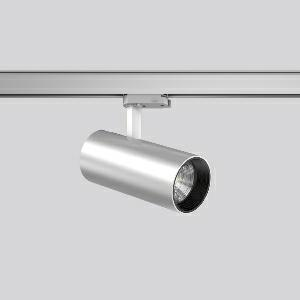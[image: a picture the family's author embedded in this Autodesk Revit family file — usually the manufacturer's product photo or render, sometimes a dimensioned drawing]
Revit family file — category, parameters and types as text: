
# Revit family: deecos_s_mini_742201_004_3_7e94
name_source: partatom
category: Lighting Fixtures
units: mm (PartAtom-declared; Revit-internal decimal feet)

## family parameters
Cut with Voids When Loaded = No
Host = Face
Light Source = No
Part Type = Normal
Room Calculation Point = No
Round Connector Dimension = Use Diameter
Shared = No

## types (1)
- DEECOS S mini (1 x LED Modul 935, 2300 lm, 3500)
    Apparent Load = 20 VA
    Approval mark = CE
    CIE Flux Codes = 80 99 100 100 100
    Color Rendering = 92
    Color Temperature = 3500
    Default Elevation = 1800 mm
    Description = Series: DEECOS S mini
LED surface-mounted projector in modern design with no visible cooling ribs. Housing: die-cast aluminium, powder-coated. Rotation range: 356°. Swivel range: 90°. Black plastic ring and recessed LED to prevent glare from the side. Optical assembly with lens made of plastic (polycarbonate) for the best homogeneous light distribution - can be changed without tools. Best colour rendering index Ra>90. With multi adaptor for 3-circuit tracks 230 V. Suitable for Track on ceiling, Wall track. High quality converter without flickering and stroboscopic effect. The following accessories can be mounted without use of tools: interchangeable lenses, decorative glasses, honeycomb louvre, clear and frosted diffusers, white interchangeable plastic ring. 
Colour: silver
Diameter: 87 mm
Height: 214 mm
Lamp: LED
Socket: without socket
Colour temperature: 3500K
Colour rendering index (CRI): 92
System power: 20 W
Rated luminous flux: 2300 lm
Luminous efficiency: 115 lm/W
Control gear: Regulated power supply
Protection class: I
Type of protection: IP 20
    Height = 214 mm
    Lamp = 1 x LED Modul 935
    Lamp Light Flux = 2300 lm
    Lamp count = 1
    Length = 87 mm
    Lifetime = 50000 h
    Luminous efficacy = 115 lm/W
    Manufacturer = RZB
    ModVariant = No
    Model = 742201.004.3
    Mounting Place = Ceiling
    Mounting Type = Rail mounted
    Number of Poles = 1
    OnlyDefault = Yes
    Power Factor = 1
    Product Name = DEECOS S mini
    Product group = Track mounted projectors
    ProductGroupID = 301
    Protection Class = Protection class I
    Protection Degree = IP 20
    RLX_Detail_Level = 1
    RLX_Emergency_Light_Flux = 0 lm
    RLX_Emergency_Type = 0
    RLX_Emergency_Type_DB = No
    RlxData = <blob elided: 37357 chars, md5=28471ab7>
    Socket = socket
    Standby Power = 0 W
    System Light Flux = 2300 lm
    System Power = 20 W
    Type Comments = Product without accessories
    Type Image = 741930.004.jpg
    URL = http://relux.com
    VarID = ---
    Voltage = 230 V
    Voltage Range = 220-240 V
    Weight = 0.00 kg
    Width = 0 mm  [stored 0 ft]

note: [stored X ft] marks values corroborated as IEEE doubles in the binary element streams (Revit-internal decimal feet)

## geometry (parser evidence)
native form markers: Blend x4, Sweep x13
no freeform markers — native parametric forms only
